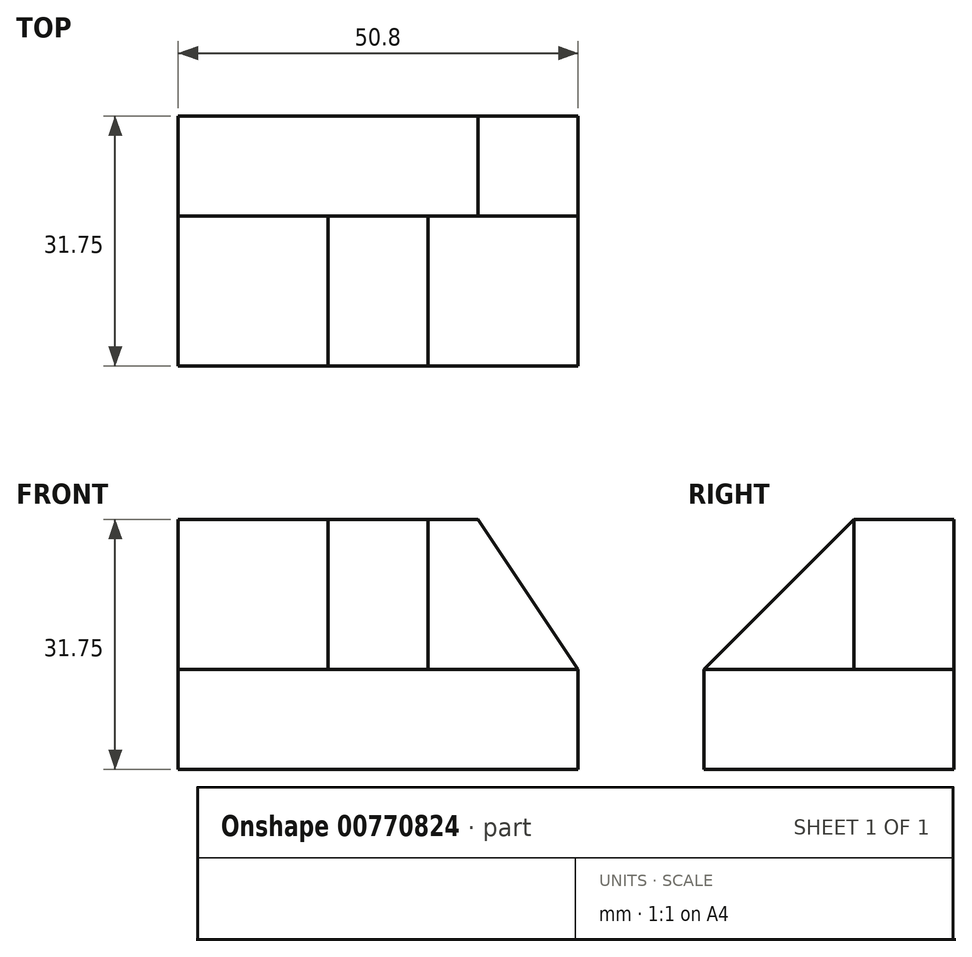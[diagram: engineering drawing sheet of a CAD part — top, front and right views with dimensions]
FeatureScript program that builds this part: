
annotation { "Feature Type Name" : "Feature", "Feature Type Description" : "" }
export const myFeature = defineFeature(function(context is Context, id is Id, definition is map)
    precondition{}
    {
        {
            var Q0;
            Q0=qCreatedBy(makeId("Front.planeOp"),FACE);
            var sketch = newSketch(context, id + "F0", { "sketchPlane" : qUnion([Q0])});
            skLineSegment(sketch, "E0", {"start": v(0, 0) * mm, "end": v(50.8, 0) * mm});
            skLineSegment(sketch, "E1", {"start": v(50.8, 0) * mm, "end": v(50.8, 31.75) * mm});
            skLineSegment(sketch, "E2", {"start": v(50.8, 31.75) * mm, "end": v(0, 31.75) * mm});
            skLineSegment(sketch, "E3", {"start": v(0, 31.75) * mm, "end": v(0, 0) * mm});
            skSolve(sketch);
        }
        {
            var Q0;
            Q0=makeQuery(id+"F0.imprint","IMPRINT",FACE,{"disambiguationData":[TD([[makeQuery(id+"F0.imprint","IMPRINT",EDGE,{"derivedFrom":sQuery(id+"F0.wireOp",EDGE,"E0")}),1.0]])]});
            extrude(context, id + "F1", {"entities" : qUnion([Q0]), "depth" : 31.75 * mm, "offsetDistance" : 25.4 * mm});
        }
        {
            var Q0;
            Q0=makeQuery(id+"F1.opExtrude","CAP_FACE",FACE,{"disambiguationData":[OSD([sQuery(id+"F0.wireOp",EDGE,"E0"),sQuery(id+"F0.wireOp",EDGE,"E1"),sQuery(id+"F0.wireOp",EDGE,"E2"),sQuery(id+"F0.wireOp",EDGE,"E3")])],"isStart":false});
            var sketch = newSketch(context, id + "F2", { "sketchPlane" : qUnion([Q0])});
            skLineSegment(sketch, "E4", {"start": v(0, 31.75) * mm, "end": v(0, 12.7) * mm});
            skLineSegment(sketch, "E5", {"start": v(0, 12.7) * mm, "end": v(19.05, 12.7) * mm});
            skLineSegment(sketch, "E6", {"start": v(19.05, 12.7) * mm, "end": v(19.05, 31.75) * mm});
            skLineSegment(sketch, "E7", {"start": v(19.05, 31.75) * mm, "end": v(0, 31.75) * mm});
            skSolve(sketch);
        }
        {
            var Q0;
            {var subQ3=sQuery(id+"F2.wireOp",EDGE,"E5");Q0=makeQuery(id+"F2.imprint","IMPRINT",FACE,{"disambiguationData":[TD([[makeQuery(id+"F2.imprint","IMPRINT",EDGE,{"derivedFrom":subQ3}),-1.0]])]});}
            var sketch = newSketch(context, id + "F3", { "sketchPlane" : qUnion([Q0])});
            skLineSegment(sketch, "E8", {"start": v(50.8, 31.75) * mm, "end": v(31.75, 31.75) * mm});
            skLineSegment(sketch, "E9", {"start": v(31.75, 31.75) * mm, "end": v(31.75, 12.7) * mm});
            skLineSegment(sketch, "E10", {"start": v(31.75, 12.7) * mm, "end": v(50.8, 12.7) * mm});
            skLineSegment(sketch, "E11", {"start": v(50.8, 31.75) * mm, "end": v(50.8, 12.7) * mm});
            skSolve(sketch);
        }
        {
            var Q0;
            Q0=makeQuery(id+"F2.imprint","IMPRINT",FACE,{"disambiguationData":[TD([[makeQuery(id+"F2.imprint","IMPRINT",EDGE,{"derivedFrom":sQuery(id+"F2.wireOp",EDGE,"E4")}),1.0]])]});
            extrude(context, id + "F4", {"entities" : qUnion([Q0]), "operationType" : NewBodyOperationType.REMOVE, "oppositeDirection" : true, "depth" : 19.05 * mm, "offsetDistance" : 25.4 * mm});
        }
        {
            var Q0;
            Q0=makeQuery(id+"F3.imprint","IMPRINT",FACE,{"disambiguationData":[TD([[makeQuery(id+"F3.imprint","IMPRINT",EDGE,{"derivedFrom":sQuery(id+"F3.wireOp",EDGE,"E8")}),1.0]])]});
            extrude(context, id + "F5", {"entities" : qUnion([Q0]), "operationType" : NewBodyOperationType.REMOVE, "oppositeDirection" : true, "depth" : 19.05 * mm, "offsetDistance" : 25.4 * mm});
        }
        {
            var Q0;
            Q0=makeQuery(id+"F5.boolean.opBoolean","COPY",FACE,{"derivedFrom":makeQuery(id+"F5.opExtrude","CAP_FACE",FACE,{"disambiguationData":[OSD([sQuery(id+"F3.wireOp",EDGE,"E8"),sQuery(id+"F3.wireOp",EDGE,"E9"),sQuery(id+"F3.wireOp",EDGE,"E10"),sQuery(id+"F3.wireOp",EDGE,"E11")])],"isStart":false})});
            var sketch = newSketch(context, id + "F6", { "sketchPlane" : qUnion([Q0])});
            skLineSegment(sketch, "E12", {"start": v(38.1, 31.75) * mm, "end": v(50.8, 12.7) * mm});
            skLineSegment(sketch, "E13", {"start": v(50.8, 12.7) * mm, "end": v(50.8, 31.75) * mm});
            skLineSegment(sketch, "E14", {"start": v(50.8, 31.75) * mm, "end": v(38.1, 31.75) * mm});
            skSolve(sketch);
        }
        {
            var Q0;
            Q0=makeQuery(id+"F6.imprint","IMPRINT",FACE,{"disambiguationData":[TD([[makeQuery(id+"F6.imprint","IMPRINT",EDGE,{"derivedFrom":sQuery(id+"F6.wireOp",EDGE,"E12")}),1.0]])]});
            extrude(context, id + "F7", {"entities" : qUnion([Q0]), "operationType" : NewBodyOperationType.REMOVE, "oppositeDirection" : true, "depth" : 12.7 * mm, "offsetDistance" : 25.4 * mm});
        }
        {
            var Q0;
            Q0=makeQuery(id+"F5.boolean.opBoolean","COPY",FACE,{"derivedFrom":makeQuery(id+"F5.opExtrude","SWEPT_FACE",FACE,{"disambiguationData":[OSD([sQuery(id+"F3.wireOp",EDGE,"E9")])]})});
            var sketch = newSketch(context, id + "F8", { "sketchPlane" : qUnion([Q0])});
            skLineSegment(sketch, "E15", {"start": v(-12.7, 31.75) * mm, "end": v(-31.75, 12.7) * mm});
            skLineSegment(sketch, "E16", {"start": v(-31.75, 12.7) * mm, "end": v(-31.75, 31.75) * mm});
            skLineSegment(sketch, "E17", {"start": v(-31.75, 31.75) * mm, "end": v(-12.7, 31.75) * mm});
            skSolve(sketch);
        }
        {
            var Q0;
            Q0=makeQuery(id+"F8.imprint","IMPRINT",FACE,{"disambiguationData":[TD([[makeQuery(id+"F8.imprint","IMPRINT",EDGE,{"derivedFrom":sQuery(id+"F8.wireOp",EDGE,"E15")}),-1.0]])]});
            extrude(context, id + "F9", {"entities" : qUnion([Q0]), "operationType" : NewBodyOperationType.REMOVE, "oppositeDirection" : true, "depth" : 12.7 * mm, "offsetDistance" : 25.4 * mm});
        }
    });
